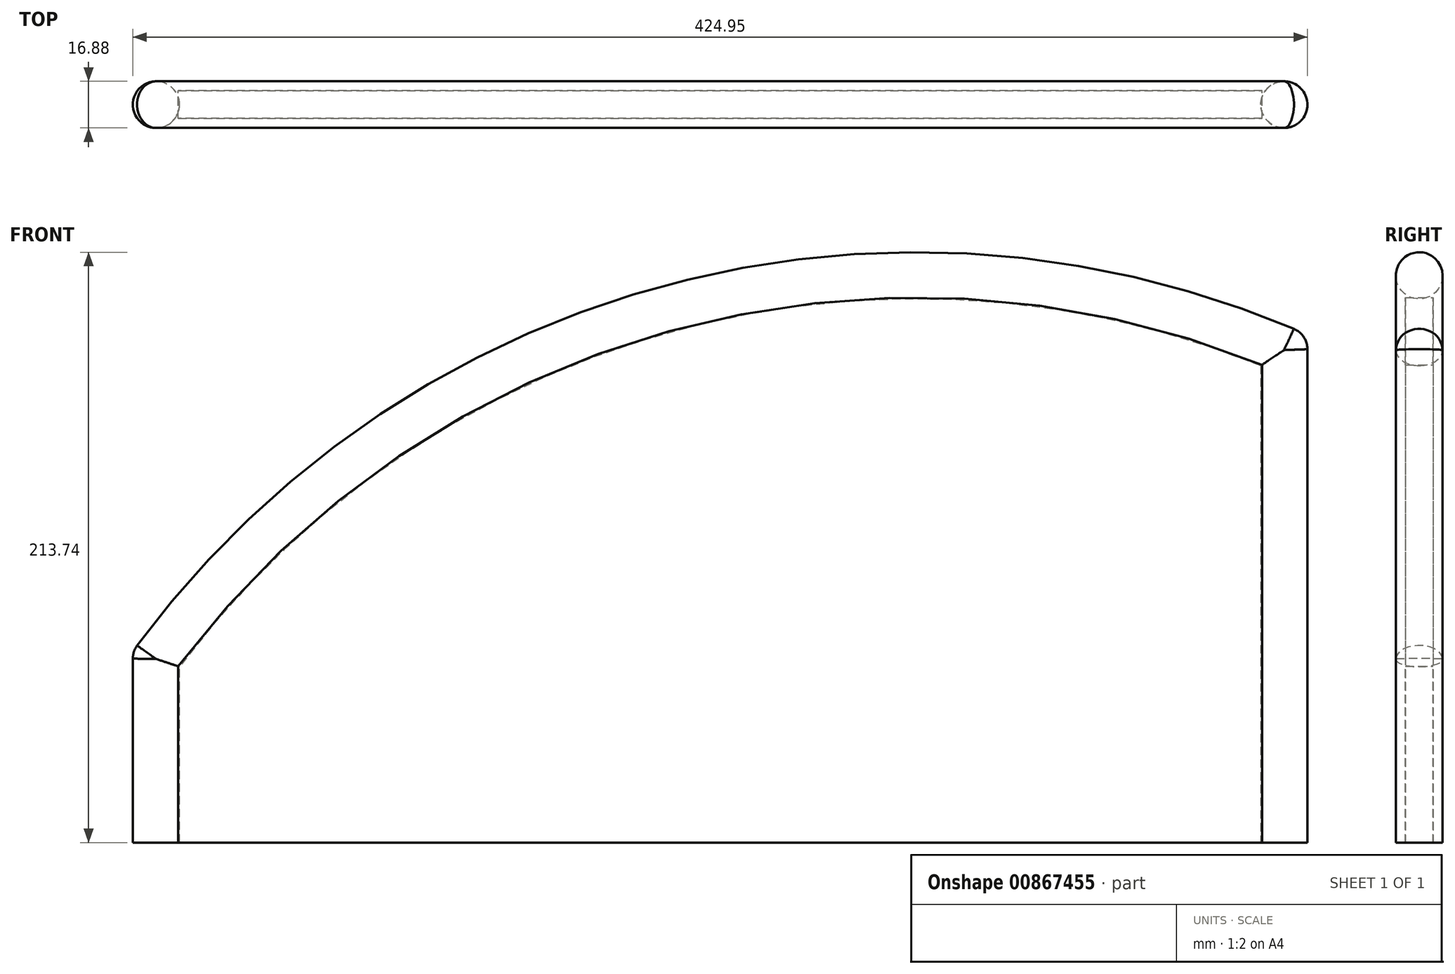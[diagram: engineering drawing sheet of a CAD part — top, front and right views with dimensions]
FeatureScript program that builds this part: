
annotation { "Feature Type Name" : "Feature", "Feature Type Description" : "" }
export const myFeature = defineFeature(function(context is Context, id is Id, definition is map)
    precondition{}
    {
        {
            var Q0;
            Q0=qCreatedBy(makeId("Top.planeOp"),FACE);
            var sketch = newSketch(context, id + "F0", { "sketchPlane" : qUnion([Q0])});
            skCircle(sketch, "E0", {"center": v(0, 0) * mm, "radius": 8.44 * mm});
            skSolve(sketch);
        }
        {
            var Q0;
            Q0=qCreatedBy(makeId("Front.planeOp"),FACE);
            var sketch = newSketch(context, id + "F1", { "sketchPlane" : qUnion([Q0])});
            skLineSegment(sketch, "E1", {"start": v(0, 0) * mm, "end": v(0, 66.45) * mm});
            skArc(sketch, "E2", {"start": v(408.07, 178.32) * mm, "mid": v(184.64, 193.14) * mm, "end": v(0, 66.45) * mm});
            skLineSegment(sketch, "E3", {"start": v(408.07, 178.32) * mm, "end": v(408.07, 0) * mm});
            skLineSegment(sketch, "E4.0", {"start": v(8, 0) * mm, "end": v(8, 63.8) * mm});
            skArc(sketch, "E4.1", {"start": v(400.07, 172.97) * mm, "mid": v(185.47, 185.07) * mm, "end": v(8, 63.8) * mm});
            skLineSegment(sketch, "E4.2", {"start": v(400.07, 172.97) * mm, "end": v(400.07, 0) * mm});
            skLineSegment(sketch, "E5", {"start": v(8, 0) * mm, "end": v(400.07, 0) * mm});
            skSolve(sketch);
        }
        {
            var Q0;
            Q0=makeQuery(id+"F0.imprint","IMPRINT",FACE,{"disambiguationData":[TD([[makeQuery(id+"F0.imprint","IMPRINT",EDGE,{"derivedFrom":sQuery(id+"F0.wireOp",EDGE,"E0")}),1.0]])]});
            var Q1;
            Q1=sQuery(id+"F1.wireOp",EDGE,"E1");
            var Q2;
            Q2=sQuery(id+"F1.wireOp",EDGE,"E2");
            var Q3;
            Q3=sQuery(id+"F1.wireOp",EDGE,"E3");
            sweep(context, id + "F2", {"profiles" : qUnion([Q0]), "path" : qUnion([Q1, Q2, Q3])});
        }
        {
            var Q0;
            Q0=makeQuery(id+"F2.opSweep","MID_CAP_EDGE",EDGE,{"disambiguationData":[OSD([sQuery(id+"F0.wireOp",EDGE,"E0"),sQuery(id+"F1.wireOp",VERTEX,"E3.start")]),OD(1.0)],"capPos":2.0});
            var Q1;
            Q1=makeQuery(id+"F2.opSweep","MID_CAP_EDGE",EDGE,{"disambiguationData":[OSD([sQuery(id+"F0.wireOp",EDGE,"E0"),sQuery(id+"F1.wireOp",VERTEX,"E2.end")]),OD(0.0)],"capPos":1.0});
            fillet(context, id + "F3", {"entities" : qUnion([Q0, Q1]), "radius" : 8 * mm, "tangentPropagation" : true, "allowEdgeOverflow" : false});
        }
        {
            var Q0;
            Q0=makeQuery(id+"F1.imprint","IMPRINT",FACE,{"disambiguationData":[TD([[makeQuery(id+"F1.imprint","IMPRINT",EDGE,{"derivedFrom":sQuery(id+"F1.wireOp",EDGE,"E4.0")}),-1.0]])]});
            extrude(context, id + "F4", {"entities" : qUnion([Q0]), "endBound" : BoundingType.SYMMETRIC, "depth" : 10 * mm, "offsetDistance" : 25 * mm});
        }
    });
